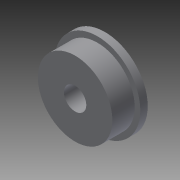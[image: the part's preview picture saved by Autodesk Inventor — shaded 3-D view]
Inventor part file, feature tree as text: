
AUTODESK INVENTOR PART (.ipt)
format: ipt  version: 2013 SP2 (Build 170200200, 200)  size: 89,600 bytes
history: native  units: mm
features: revolve x1, sketch x1
ambient origin geometry x8: Origin, YZ Plane, XZ Plane, XY Plane, X Axis, Y Axis, Z Axis, Center Point
bodies: Solid1 (feature_tree)
feature tree (2):
  revolve  "Revolution1"  [1 undecoded]
  sketch  "Sketch1"  dims[d0=1.5mm d1=5.0mm d2=0.75mm d3=4.0mm d4=1.0mm d5=90.0deg]
note: 1 required parameter value undecoded (feature->parameter linkage not recoverable at this tier; creation-order binding heuristic only, values carry confidence <= 0.55)
